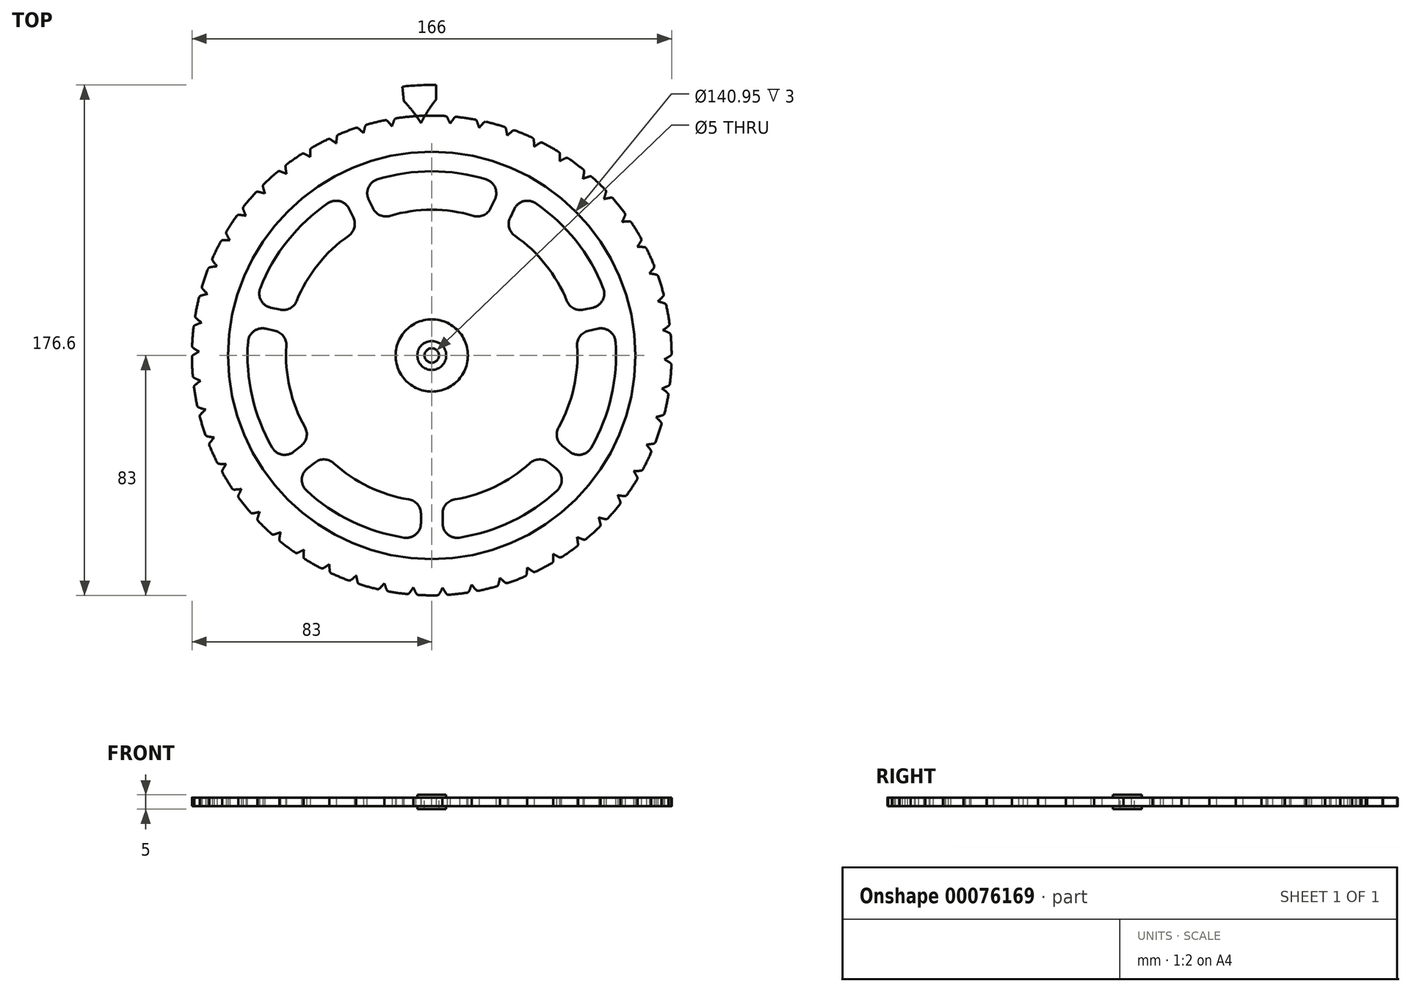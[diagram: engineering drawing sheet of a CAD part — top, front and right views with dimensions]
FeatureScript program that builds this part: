
annotation { "Feature Type Name" : "Feature", "Feature Type Description" : "" }
export const myFeature = defineFeature(function(context is Context, id is Id, definition is map)
    precondition{}
    {
        {
            assignVariable(context, id + "F0", {"name" : "Mod", "anyValue" : 3 * mm});
        }
        {
            assignVariable(context, id + "F1", {"name" : "T", "anyValue" : 50});
        }
        {
            var Q0;
            Q0=qCreatedBy(makeId("Top.planeOp"),FACE);
            var sketch = newSketch(context, id + "F2", { "sketchPlane" : qUnion([Q0])});
            skCircle(sketch, "E0", {"center": v(0, 0) * mm, "radius": 70.48 * mm, "construction": true});
            skLineSegment(sketch, "E1", {"start": v(0, 0) * mm, "end": v(0, 70.48) * mm, "construction": true});
            skLineSegment(sketch, "E2.1.0", {"start": v(0, 0) * mm, "end": v(-3.07, 70.4) * mm, "construction": true});
            skLineSegment(sketch, "E2.2.0", {"start": v(0, 0) * mm, "end": v(-6.14, 70.2) * mm, "construction": true});
            skLineSegment(sketch, "E2.3.0", {"start": v(0, 0) * mm, "end": v(-9.2, 69.87) * mm, "construction": true});
            skLineSegment(sketch, "E2.4.0", {"start": v(0, 0) * mm, "end": v(-12.24, 69.4) * mm, "construction": true});
            skLineSegment(sketch, "E2.5.0", {"start": v(0, 0) * mm, "end": v(-15.25, 68.8) * mm, "construction": true});
            skLineSegment(sketch, "E2.6.0", {"start": v(0, 0) * mm, "end": v(-18.24, 68.08) * mm, "construction": true});
            skLineSegment(sketch, "E2.7.0", {"start": v(0, 0) * mm, "end": v(-21.2, 67.22) * mm, "construction": true});
            skLineSegment(sketch, "E2.8.0", {"start": v(0, 0) * mm, "end": v(-24.1, 66.23) * mm, "construction": true});
            skLineSegment(sketch, "E2.9.0", {"start": v(0, 0) * mm, "end": v(-26.97, 65.11) * mm, "construction": true});
            skLineSegment(sketch, "E2.10.0", {"start": v(0, 0) * mm, "end": v(-29.78, 63.87) * mm, "construction": true});
            skLineSegment(sketch, "E2.11.0", {"start": v(0, 0) * mm, "end": v(-32.54, 62.51) * mm, "construction": true});
            skLineSegment(sketch, "E2.12.0", {"start": v(0, 0) * mm, "end": v(-35.24, 61.03) * mm, "construction": true});
            skLineSegment(sketch, "E2.13.0", {"start": v(0, 0) * mm, "end": v(-37.87, 59.44) * mm, "construction": true});
            skLineSegment(sketch, "E2.14.0", {"start": v(0, 0) * mm, "end": v(-40.42, 57.73) * mm, "construction": true});
            skLineSegment(sketch, "E2.15.0", {"start": v(0, 0) * mm, "end": v(-42.9, 55.91) * mm, "construction": true});
            skLineSegment(sketch, "E2.16.0", {"start": v(0, 0) * mm, "end": v(-45.3, 53.99) * mm, "construction": true});
            skLineSegment(sketch, "E2.17.0", {"start": v(0, 0) * mm, "end": v(-47.61, 51.96) * mm, "construction": true});
            skLineSegment(sketch, "E2.18.0", {"start": v(0, 0) * mm, "end": v(-49.83, 49.83) * mm, "construction": true});
            skLineSegment(sketch, "E2.19.0", {"start": v(0, 0) * mm, "end": v(-51.96, 47.61) * mm, "construction": true});
            skLineSegment(sketch, "E2.20.0", {"start": v(0, 0) * mm, "end": v(-53.99, 45.3) * mm, "construction": true});
            skLineSegment(sketch, "E2.21.0", {"start": v(0, 0) * mm, "end": v(-55.91, 42.9) * mm, "construction": true});
            skLineSegment(sketch, "E2.22.0", {"start": v(0, 0) * mm, "end": v(-57.73, 40.42) * mm, "construction": true});
            skLineSegment(sketch, "E2.23.0", {"start": v(0, 0) * mm, "end": v(-59.44, 37.87) * mm, "construction": true});
            skLineSegment(sketch, "E2.24.0", {"start": v(0, 0) * mm, "end": v(-61.03, 35.24) * mm, "construction": true});
            skLineSegment(sketch, "E2.anchor2", {"start": v(0, 0) * mm, "end": v(-67.22, 21.2) * mm, "construction": true});
            skLineSegment(sketch, "E3", {"start": v(-3.07, 70.4) * mm, "end": v(0, 70.54) * mm, "construction": true});
            skLineSegment(sketch, "E4", {"start": v(-6.14, 70.2) * mm, "end": v(-0.02, 70.74) * mm, "construction": true});
            skLineSegment(sketch, "E5", {"start": v(-9.2, 69.87) * mm, "end": v(-0.05, 71.08) * mm, "construction": true});
            skLineSegment(sketch, "E6", {"start": v(-12.24, 69.4) * mm, "end": v(-0.12, 71.54) * mm, "construction": true});
            skLineSegment(sketch, "E7", {"start": v(-15.25, 68.8) * mm, "end": v(-0.24, 72.13) * mm, "construction": true});
            skLineSegment(sketch, "E8", {"start": v(-18.24, 68.08) * mm, "end": v(-0.42, 72.85) * mm, "construction": true});
            skLineSegment(sketch, "E9", {"start": v(-21.2, 67.22) * mm, "end": v(-0.66, 73.69) * mm, "construction": true});
            skLineSegment(sketch, "E10", {"start": v(-24.1, 66.23) * mm, "end": v(-0.99, 74.64) * mm, "construction": true});
            skLineSegment(sketch, "E11", {"start": v(-26.97, 65.11) * mm, "end": v(-1.4, 75.7) * mm, "construction": true});
            skLineSegment(sketch, "E12", {"start": v(-29.78, 63.87) * mm, "end": v(-1.91, 76.87) * mm, "construction": true});
            skLineSegment(sketch, "E13", {"start": v(-32.54, 62.51) * mm, "end": v(-2.54, 78.13) * mm, "construction": true});
            skLineSegment(sketch, "E14", {"start": v(-35.24, 61.03) * mm, "end": v(-3.28, 79.49) * mm, "construction": true});
            skLineSegment(sketch, "E15", {"start": v(-37.87, 59.44) * mm, "end": v(-4.15, 80.92) * mm, "construction": true});
            skLineSegment(sketch, "E16", {"start": v(-40.42, 57.73) * mm, "end": v(-5.16, 82.42) * mm, "construction": true});
            skLineSegment(sketch, "E17", {"start": v(-42.9, 55.91) * mm, "end": v(-6.3, 84) * mm, "construction": true});
            skLineSegment(sketch, "E18", {"start": v(-45.3, 53.99) * mm, "end": v(-7.61, 85.62) * mm, "construction": true});
            skLineSegment(sketch, "E19", {"start": v(-47.61, 51.96) * mm, "end": v(-9.07, 87.28) * mm, "construction": true});
            skLineSegment(sketch, "E20", {"start": v(-49.83, 49.83) * mm, "end": v(-10.7, 88.97) * mm, "construction": true});
            skLineSegment(sketch, "E21", {"start": v(-51.96, 47.61) * mm, "end": v(-12.49, 90.7) * mm, "construction": true});
            skLineSegment(sketch, "E22", {"start": v(-53.99, 45.3) * mm, "end": v(-14.46, 92.42) * mm, "construction": true});
            skLineSegment(sketch, "E23", {"start": v(-55.91, 42.9) * mm, "end": v(-16.6, 94.14) * mm, "construction": true});
            skLineSegment(sketch, "E24", {"start": v(-57.73, 40.42) * mm, "end": v(-18.93, 95.84) * mm, "construction": true});
            skLineSegment(sketch, "E25", {"start": v(-59.44, 37.87) * mm, "end": v(-21.44, 97.52) * mm, "construction": true});
            skCircle(sketch, "E26", {"center": v(0, 0) * mm, "radius": 75 * mm});
            skCircle(sketch, "E27", {"center": v(0, 0) * mm, "radius": 78 * mm});
            skPoint(sketch, "E28", {"position": v(-1.12, 75) * mm});
            skLineSegment(sketch, "E29", {"start": v(-1.12, 75) * mm, "end": v(0, 0) * mm, "construction": true});
            skLineSegment(sketch, "E30", {"start": v(-3.61, 77.92) * mm, "end": v(0, 0) * mm, "construction": true});
            skLineSegment(sketch, "E31", {"start": v(-6.52, 70.17) * mm, "end": v(0, 0) * mm, "construction": true});
            skLineSegment(sketch, "E32.2.25.0", {"start": v(0, 0) * mm, "end": v(-62.51, 32.54) * mm, "construction": true});
            skLineSegment(sketch, "E32.2.26.0", {"start": v(0, 0) * mm, "end": v(-63.87, 29.78) * mm, "construction": true});
            skLineSegment(sketch, "E32.2.27.0", {"start": v(0, 0) * mm, "end": v(-65.11, 26.97) * mm, "construction": true});
            skLineSegment(sketch, "E32.2.28.0", {"start": v(0, 0) * mm, "end": v(-66.23, 24.1) * mm, "construction": true});
            skLineSegment(sketch, "E33", {"start": v(-61.03, 35.24) * mm, "end": v(-24.13, 99.15) * mm, "construction": true});
            skLineSegment(sketch, "E34", {"start": v(-62.51, 32.54) * mm, "end": v(-27.02, 100.73) * mm, "construction": true});
            skLineSegment(sketch, "E35", {"start": v(-63.87, 29.78) * mm, "end": v(-30.08, 102.25) * mm, "construction": true});
            skLineSegment(sketch, "E36", {"start": v(-65.11, 26.97) * mm, "end": v(-33.34, 103.68) * mm, "construction": true});
            skLineSegment(sketch, "E37", {"start": v(-66.23, 24.1) * mm, "end": v(-36.78, 105.02) * mm, "construction": true});
            skLineSegment(sketch, "E38", {"start": v(-67.22, 21.2) * mm, "end": v(-40.4, 106.24) * mm, "construction": true});
            skFitSpline(sketch, "E39", {"points": [v(0, 70.48) * mm, v(0, 70.54) * mm, v(-0.02, 70.74) * mm, v(-0.05, 71.08) * mm, v(-0.12, 71.54) * mm, v(-0.24, 72.13) * mm, v(-0.42, 72.85) * mm, v(-0.66, 73.69) * mm, v(-0.99, 74.64) * mm, v(-1.4, 75.7) * mm, v(-1.91, 76.87) * mm, v(-2.54, 78.13) * mm, v(-3.28, 79.49) * mm, v(-4.15, 80.92) * mm, v(-5.16, 82.42) * mm, v(-6.3, 84) * mm, v(-7.61, 85.62) * mm, v(-9.07, 87.28) * mm, v(-10.7, 88.97) * mm, v(-12.49, 90.7) * mm, v(-14.46, 92.42) * mm, v(-16.6, 94.14) * mm, v(-18.93, 95.84) * mm, v(-21.44, 97.52) * mm, v(-24.13, 99.15) * mm, v(-27.02, 100.73) * mm, v(-30.08, 102.25) * mm, v(-33.34, 103.68) * mm, v(-36.78, 105.02) * mm, v(-40.4, 106.24) * mm], "startDerivative": vector(-0.86, 29.64) * mm, "endDerivative": vector(-211.97, 71.92) * mm, "construction": true});
            skFitSpline(sketch, "E40.MirrorCS", {"points": [v(-6.52, 70.17) * mm, v(-6.52, 70.24) * mm, v(-6.53, 70.44) * mm, v(-6.52, 70.78) * mm, v(-6.5, 71.25) * mm, v(-6.43, 71.85) * mm, v(-6.32, 72.58) * mm, v(-6.16, 73.43) * mm, v(-5.92, 74.41) * mm, v(-5.6, 75.5) * mm, v(-5.2, 76.72) * mm, v(-4.7, 78.03) * mm, v(-4.09, 79.45) * mm, v(-3.35, 80.96) * mm, v(-2.49, 82.55) * mm, v(-1.49, 84.22) * mm, v(-0.34, 85.95) * mm, v(0.96, 87.74) * mm, v(2.42, 89.58) * mm, v(4.04, 91.46) * mm, v(5.84, 93.36) * mm, v(7.82, 95.27) * mm, v(9.98, 97.18) * mm, v(12.32, 99.08) * mm, v(14.86, 100.96) * mm, v(17.58, 102.8) * mm, v(20.5, 104.6) * mm, v(23.6, 106.32) * mm, v(26.9, 107.97) * mm, v(30.4, 109.53) * mm], "startDerivative": vector(-1.88, 29.59) * mm, "endDerivative": vector(204.4, 91.22) * mm, "construction": true});
            skFitSpline(sketch, "E41.0", {"points": [v(-6.9, 84.29) * mm, v(-6.9, 84.34) * mm, v(-6.9, 84.36) * mm, v(-6.9, 84.36) * mm, v(-6.9, 84.38) * mm, v(-6.9, 84.43) * mm, v(-6.9, 84.53) * mm, v(-6.9, 84.64) * mm, v(-6.9, 84.77) * mm, v(-6.9, 84.94) * mm, v(-6.88, 85.16) * mm, v(-6.86, 85.4) * mm, v(-6.84, 85.67) * mm, v(-6.8, 86.03) * mm, v(-6.74, 86.5) * mm, v(-6.64, 87.12) * mm, v(-6.5, 87.76) * mm, v(-6.3, 88.66) * mm, v(-6, 89.84) * mm, v(-5.52, 91.34) * mm, v(-4.95, 92.89) * mm, v(-4.27, 94.5) * mm, v(-3.5, 96.13) * mm, v(-2.34, 98.36) * mm, v(-0.65, 101.19) * mm, v(1.75, 104.61) * mm, v(4.5, 108.02) * mm, v(7.1, 110.82) * mm, v(9.33, 113) * mm, v(11.1, 114.63) * mm, v(12.93, 116.22) * mm, v(14.85, 117.78) * mm, v(16.84, 119.3) * mm, v(18.91, 120.79) * mm, v(20.68, 121.99) * mm, v(22.15, 122.93) * mm, v(23.28, 123.63) * mm, v(24.42, 124.32) * mm, v(25.37, 124.88) * mm, v(26.12, 125.3) * mm, v(26.85, 125.73) * mm, v(27.6, 126.14) * mm, v(28.38, 126.56) * mm, v(29, 126.9) * mm, v(29.68, 127.23) * mm, v(30.4, 127.6) * mm, v(31.14, 127.96) * mm, v(31.86, 128.3) * mm, v(32.52, 128.63) * mm, v(33.1, 128.9) * mm, v(33.47, 129.08) * mm, v(33.69, 129.18) * mm, v(33.85, 129.26) * mm, v(33.98, 129.32) * mm, v(34.16, 129.4) * mm, v(34.5, 129.54) * mm, v(35.34, 129.9) * mm, v(36.59, 130.44) * mm, v(37.87, 131) * mm]});
            skFitSpline(sketch, "E42.0", {"points": [v(-0.05, 84.57) * mm, v(-0.05, 84.62) * mm, v(-0.05, 84.64) * mm, v(-0.05, 84.64) * mm, v(-0.05, 84.66) * mm, v(-0.06, 84.71) * mm, v(-0.06, 84.81) * mm, v(-0.07, 84.92) * mm, v(-0.08, 85.05) * mm, v(-0.1, 85.22) * mm, v(-0.13, 85.44) * mm, v(-0.17, 85.68) * mm, v(-0.22, 85.94) * mm, v(-0.28, 86.3) * mm, v(-0.39, 86.77) * mm, v(-0.54, 87.37) * mm, v(-0.72, 88) * mm, v(-0.99, 88.88) * mm, v(-1.4, 90.03) * mm, v(-2, 91.48) * mm, v(-2.7, 92.98) * mm, v(-3.5, 94.52) * mm, v(-4.4, 96.1) * mm, v(-5.74, 98.22) * mm, v(-7.65, 100.9) * mm, v(-10.33, 104.12) * mm, v(-13.36, 107.29) * mm, v(-16.17, 109.86) * mm, v(-18.58, 111.86) * mm, v(-20.46, 113.33) * mm, v(-22.43, 114.76) * mm, v(-24.47, 116.16) * mm, v(-26.58, 117.52) * mm, v(-28.76, 118.83) * mm, v(-30.63, 119.88) * mm, v(-32.16, 120.7) * mm, v(-33.35, 121.3) * mm, v(-34.55, 121.9) * mm, v(-35.54, 122.38) * mm, v(-36.31, 122.74) * mm, v(-37.08, 123.1) * mm, v(-37.85, 123.45) * mm, v(-38.67, 123.8) * mm, v(-39.32, 124.08) * mm, v(-40.02, 124.37) * mm, v(-40.77, 124.67) * mm, v(-41.53, 124.97) * mm, v(-42.28, 125.26) * mm, v(-42.97, 125.52) * mm, v(-43.56, 125.75) * mm, v(-43.95, 125.9) * mm, v(-44.18, 125.98) * mm, v(-44.34, 126.04) * mm, v(-44.48, 126.1) * mm, v(-44.67, 126.16) * mm, v(-45.02, 126.28) * mm, v(-45.88, 126.56) * mm, v(-47.17, 127) * mm, v(-48.5, 127.45) * mm]});
            skArc(sketch, "E43", {"start": v(-0.13, 71.25) * mm, "mid": v(-3.3, 71.17) * mm, "end": v(-6.46, 70.96) * mm});
            skArc(sketch, "E44", {"start": v(-6.72, 70.93) * mm, "mid": v(3.3, -71.17) * mm, "end": v(0.13, 71.25) * mm});
            skPoint(sketch, "E45.visualSharp", {"position": v(-6.46, 70.96) * mm});
            skArc(sketch, "E45.filletArc", {"start": v(-6.72, 70.93) * mm, "mid": v(-6.53, 71.02) * mm, "end": v(-6.45, 71.2) * mm});
            skPoint(sketch, "E46.visualSharp", {"position": v(-0.13, 71.25) * mm});
            skArc(sketch, "E46.filletArc", {"start": v(-0.17, 71.5) * mm, "mid": v(-0.07, 71.32) * mm, "end": v(0.13, 71.25) * mm});
            skArc(sketch, "E47", {"start": v(-6.72, 70.93) * mm, "mid": v(-3.3, 71.17) * mm, "end": v(0.13, 71.25) * mm});
            skSolve(sketch);
        }
        {
            assignVariable(context, id + "F3", {"name" : "Thickness", "anyValue" : 3 * mm});
        }
        {
            var Q0;
            {var subQ0=sQuery(id+"F2.wireOp",EDGE,"E44");Q0=makeQuery(id+"F2.imprint","IMPRINT",FACE,{"disambiguationData":[TD([[makeQuery(id+"F2.imprint","IMPRINT",EDGE,{"derivedFrom":subQ0}),1.0]])]});}
            extrude(context, id + "F4", {"entities" : qUnion([Q0]), "endBound" : BoundingType.SYMMETRIC, "depth" : getVariable(context, 'Thickness')});
        }
        {
            var Q0;
            {var subQ0=sQuery(id+"F2.wireOp",EDGE,"E41.0");var subQ1=sQuery(id+"F2.wireOp",EDGE,"E26");var subQ2=makeQuery(id+"F2.imprint","INTERSECT",VERTEX,{"derivedFrom":[subQ1,subQ0]});Q0=makeQuery(id+"F2.imprint","IMPRINT",FACE,{"disambiguationData":[TD([[makeQuery(id+"F2.imprint","IMPRINT",EDGE,{"disambiguationData":[TD([[subQ2,1.0]])],"derivedFrom":subQ1}),-1.0]])]});}
            var Q1;
            {var subQ0=sQuery(id+"F2.wireOp",EDGE,"E45.filletArc");Q1=makeQuery(id+"F2.imprint","IMPRINT",FACE,{"disambiguationData":[TD([[makeQuery(id+"F2.imprint","IMPRINT",EDGE,{"derivedFrom":subQ0}),-1.0]])]});}
            extrude(context, id + "F5", {"entities" : qUnion([Q0, Q1]), "endBound" : BoundingType.SYMMETRIC, "oppositeDirection" : true, "depth" : getVariable(context, 'Thickness')});
        }
        {
            var Q0;
            Q0=qCreatedBy(makeId("Front.planeOp"),FACE);
            var sketch = newSketch(context, id + "F6", { "sketchPlane" : qUnion([Q0])});
            skLineSegment(sketch, "E48", {"start": v(0, 0) * mm, "end": v(0, 11.67) * mm});
            skSolve(sketch);
        }
        {
            var Q0;
            Q0=makeQuery(id+"F5.opExtrude","SWEPT_BODY",BODY,{"disambiguationData":[OSD([sQuery(id+"F2.wireOp",EDGE,"4a69cfca-a3bc-48ab-be35-960da39a462e"),sQuery(id+"F2.wireOp",EDGE,"Aigjkfxe-bQmJ-sPwt-LIfV-hiAVdCM8k71b"),sQuery(id+"F2.wireOp",EDGE,"E27"),sQuery(id+"F2.wireOp",EDGE,"abf2ab3a-d2cd-41dc-bda2-9d514d4bd3180.MirrorCS"),sQuery(id+"F2.wireOp",EDGE,"dKfRnCup-fbZC-EHfO-hmoI-6kX9ckiFD719"),sQuery(id+"F2.wireOp",EDGE,"V1zgMlGZ-DbEQ-ZBOL-SlYs-zCFJA2V7msXA")])]});
            var Q1;
            Q1=sQuery(id+"F6.wireOp",EDGE,"E48");
            circularPattern(context, id + "F7", {"operationType" : NewBodyOperationType.ADD, "entities" : qUnion([Q0]), "axis" : qUnion([Q1]), "angle" : 360 * degree, "instanceCount" : getVariable(context, 'T'), "equalSpace" : true});
        }
        {
            var Q0;
            Q0=qCreatedBy(makeId("Top.planeOp"),FACE);
            var sketch = newSketch(context, id + "F8", { "sketchPlane" : qUnion([Q0])});
            skCircle(sketch, "E49", {"center": v(0, 0) * mm, "radius": 71.25 * mm});
            skCircle(sketch, "E50", {"center": v(0, 0) * mm, "radius": 2.5 * mm});
            skCircle(sketch, "E51", {"center": v(0, 0) * mm, "radius": 5 * mm});
            skCircle(sketch, "E52.0", {"center": v(0, 0) * mm, "radius": 63.75 * mm, "construction": true});
            skCircle(sketch, "E53.0", {"center": v(0, 0) * mm, "radius": 12.5 * mm, "construction": true});
            skLineSegment(sketch, "E54", {"start": v(0, 0) * mm, "end": v(30.91, 64.2) * mm, "construction": true});
            skLineSegment(sketch, "E55", {"start": v(2.68, 14.2) * mm, "end": v(6.09, 21.28) * mm});
            skArc(sketch, "E56", {"start": v(0, 12.5) * mm, "mid": v(0.01, -12.5) * mm, "end": v(-0.02, 12.5) * mm});
            skArc(sketch, "E57", {"start": v(0, 63.75) * mm, "mid": v(9.5, 63.04) * mm, "end": v(18.8, 60.92) * mm});
            skPoint(sketch, "E58.visualSharp", {"position": v(24.23, 58.96) * mm});
            skPoint(sketch, "E59.visualSharp", {"position": v(1.8, 12.37) * mm});
            skArc(sketch, "E59.filletArc", {"start": v(-0.02, 12.5) * mm, "mid": v(1.57, 12.96) * mm, "end": v(2.68, 14.2) * mm});
            skCircle(sketch, "E60", {"center": v(0, 0) * mm, "radius": 46.67 * mm, "construction": true});
            skPoint(sketch, "E61", {"position": v(0, 46.67) * mm});
            skArc(sketch, "E62", {"start": v(0, 50.42) * mm, "mid": v(7.3, 49.89) * mm, "end": v(14.43, 48.3) * mm});
            skLineSegment(sketch, "E63", {"start": v(18.44, 46.93) * mm, "end": v(18.44, 46.93) * mm});
            skLineSegment(sketch, "E64", {"start": v(20.36, 50.93) * mm, "end": v(21.83, 53.97) * mm});
            skPoint(sketch, "E65.visualSharp", {"position": v(18.44, 46.93) * mm});
            skArc(sketch, "E65.filletArc", {"start": v(14.43, 48.3) * mm, "mid": v(17.88, 48.53) * mm, "end": v(20.36, 50.93) * mm});
            skLineSegment(sketch, "E66", {"start": v(0, 12.5) * mm, "end": v(0, 29.58) * mm, "construction": true});
            skLineSegment(sketch, "E67", {"start": v(0, 29.58) * mm, "end": v(0, 46.67) * mm, "construction": true});
            skLineSegment(sketch, "E68", {"start": v(0, 46.67) * mm, "end": v(0, 63.75) * mm, "construction": true});
            skCircle(sketch, "E69", {"center": v(0, 0) * mm, "radius": 29.58 * mm, "construction": true});
            skArc(sketch, "E70", {"start": v(0, 25.83) * mm, "mid": v(1.92, 25.76) * mm, "end": v(3.83, 25.55) * mm});
            skPoint(sketch, "E71.visualSharp", {"position": v(7.71, 24.66) * mm});
            skArc(sketch, "E71.filletArc", {"start": v(6.09, 21.28) * mm, "mid": v(6.03, 23.98) * mm, "end": v(3.83, 25.55) * mm});
            skLineSegment(sketch, "E72", {"start": v(3.75, 38.14) * mm, "end": v(3.75, 36.52) * mm});
            skArc(sketch, "E73", {"start": v(6.92, 32.6) * mm, "mid": v(10.77, 31.55) * mm, "end": v(14.46, 30.03) * mm});
            skArc(sketch, "E74", {"start": v(8.55, 42.06) * mm, "mid": v(13.69, 40.67) * mm, "end": v(18.62, 38.67) * mm});
            skPoint(sketch, "E75.visualSharp", {"position": v(3.75, 33.12) * mm});
            skArc(sketch, "E75.filletArc", {"start": v(3.75, 36.52) * mm, "mid": v(4.64, 34) * mm, "end": v(6.92, 32.6) * mm});
            skPoint(sketch, "E76.visualSharp", {"position": v(3.75, 42.75) * mm});
            skArc(sketch, "E76.filletArc", {"start": v(8.55, 42.06) * mm, "mid": v(5.22, 41.23) * mm, "end": v(3.75, 38.14) * mm});
            skArc(sketch, "E77.MirrorCS", {"start": v(-14.43, 48.3) * mm, "mid": v(-17.88, 48.53) * mm, "end": v(-20.36, 50.93) * mm});
            skArc(sketch, "E78.MirrorCS", {"start": v(0, 50.42) * mm, "mid": v(-7.3, 49.89) * mm, "end": v(-14.43, 48.3) * mm});
            skArc(sketch, "E79.MirrorCS", {"start": v(-8.55, 42.06) * mm, "mid": v(-13.69, 40.67) * mm, "end": v(-18.62, 38.67) * mm});
            skArc(sketch, "E80.MirrorCS", {"start": v(-8.55, 42.06) * mm, "mid": v(-5.22, 41.23) * mm, "end": v(-3.75, 38.14) * mm});
            skLineSegment(sketch, "E81.MirrorCS", {"start": v(-3.75, 38.14) * mm, "end": v(-3.75, 36.52) * mm});
            skArc(sketch, "E82.MirrorCS", {"start": v(-3.75, 36.52) * mm, "mid": v(-4.64, 34) * mm, "end": v(-6.92, 32.6) * mm});
            skArc(sketch, "E83.MirrorCS", {"start": v(-6.92, 32.6) * mm, "mid": v(-10.77, 31.55) * mm, "end": v(-14.46, 30.03) * mm});
            skArc(sketch, "E84.MirrorCS", {"start": v(-6.09, 21.28) * mm, "mid": v(-6.03, 23.98) * mm, "end": v(-3.83, 25.55) * mm});
            skArc(sketch, "E85.MirrorCS", {"start": v(0, 25.83) * mm, "mid": v(-1.92, 25.76) * mm, "end": v(-3.83, 25.55) * mm});
            skLineSegment(sketch, "E86.MirrorCS", {"start": v(-2.68, 14.2) * mm, "end": v(-6.09, 21.28) * mm});
            skArc(sketch, "E87.MirrorCS", {"start": v(0.02, 12.5) * mm, "mid": v(-1.57, 12.96) * mm, "end": v(-2.68, 14.2) * mm});
            skArc(sketch, "E88.MirrorCS", {"start": v(0, 12.5) * mm, "mid": v(-0.01, -12.5) * mm, "end": v(0.02, 12.5) * mm});
            skArc(sketch, "E89.filletArc", {"start": v(21.83, 53.97) * mm, "mid": v(21.9, 58.14) * mm, "end": v(18.8, 60.92) * mm});
            skArc(sketch, "E90.MirrorCS", {"start": v(-21.83, 53.97) * mm, "mid": v(-21.9, 58.14) * mm, "end": v(-18.8, 60.92) * mm});
            skArc(sketch, "E91.MirrorCS", {"start": v(0, 63.75) * mm, "mid": v(-9.5, 63.04) * mm, "end": v(-18.8, 60.92) * mm});
            skLineSegment(sketch, "E92.MirrorCS", {"start": v(-20.36, 50.93) * mm, "end": v(-21.83, 53.97) * mm});
            skPoint(sketch, "E93.1.0", {"position": v(-31, 55.71) * mm});
            skArc(sketch, "E93.1.1", {"start": v(-38.21, 19.54) * mm, "mid": v(-40.34, 14.66) * mm, "end": v(-41.84, 9.55) * mm});
            skLineSegment(sketch, "E93.1.2", {"start": v(-23.13, 18.44) * mm, "end": v(-36.49, 29.1) * mm, "construction": true});
            skLineSegment(sketch, "E93.1.3", {"start": v(-36.49, 29.1) * mm, "end": v(-49.84, 39.75) * mm, "construction": true});
            skArc(sketch, "E93.1.4", {"start": v(-39.42, 31.43) * mm, "mid": v(-34.46, 36.8) * mm, "end": v(-28.77, 41.4) * mm});
            skArc(sketch, "E93.1.5", {"start": v(-29.8, 14.92) * mm, "mid": v(-31.38, 11.25) * mm, "end": v(-32.5, 7.42) * mm});
            skArc(sketch, "E93.1.6", {"start": v(-20.2, 16.1) * mm, "mid": v(-21.34, 14.56) * mm, "end": v(-22.36, 12.94) * mm});
            skLineSegment(sketch, "E93.1.7", {"start": v(-12.77, 6.76) * mm, "end": v(-20.43, 8.5) * mm});
            skLineSegment(sketch, "E93.1.8", {"start": v(-32.15, 20.85) * mm, "end": v(-30.9, 19.84) * mm});
            skArc(sketch, "E93.1.9", {"start": v(-55.8, 16.58) * mm, "mid": v(-59.11, 19.12) * mm, "end": v(-59.35, 23.28) * mm});
            skPoint(sketch, "E93.1.10", {"position": v(-25.2, 43.67) * mm});
            skArc(sketch, "E93.1.11", {"start": v(-49.84, 39.75) * mm, "mid": v(-55.21, 31.87) * mm, "end": v(-59.35, 23.28) * mm});
            skArc(sketch, "E93.1.12", {"start": v(-39.42, 31.43) * mm, "mid": v(-43.55, 25.4) * mm, "end": v(-46.76, 18.84) * mm});
            skPoint(sketch, "E93.1.13", {"position": v(-31.09, 29.59) * mm});
            skLineSegment(sketch, "E93.1.14", {"start": v(-9.77, 7.8) * mm, "end": v(-23.13, 18.44) * mm, "construction": true});
            skArc(sketch, "E93.1.15", {"start": v(-27.55, 32.9) * mm, "mid": v(-23.27, 36.06) * mm, "end": v(-18.62, 38.67) * mm});
            skPoint(sketch, "E93.1.16", {"position": v(-36.49, 29.1) * mm});
            skLineSegment(sketch, "E93.1.17", {"start": v(-9.43, 10.94) * mm, "end": v(-12.84, 18.03) * mm});
            skArc(sketch, "E93.1.18", {"start": v(-49.84, 39.75) * mm, "mid": v(-43.36, 46.73) * mm, "end": v(-35.9, 52.68) * mm});
            skLineSegment(sketch, "E93.1.19", {"start": v(-52.52, 15.83) * mm, "end": v(-55.8, 16.58) * mm});
            skPoint(sketch, "E93.1.20", {"position": v(-14.47, 21.4) * mm});
            skArc(sketch, "E93.1.21", {"start": v(-21.18, 25.74) * mm, "mid": v(-17.95, 28.09) * mm, "end": v(-14.46, 30.03) * mm});
            skPoint(sketch, "E93.1.22", {"position": v(-8.55, 9.12) * mm});
            skPoint(sketch, "E93.1.23", {"position": v(-23.56, 23.58) * mm});
            skArc(sketch, "E93.1.24", {"start": v(-28.77, 41.4) * mm, "mid": v(-26.8, 44.23) * mm, "end": v(-27.12, 47.68) * mm});
            skLineSegment(sketch, "E93.1.25", {"start": v(-27.48, 26.71) * mm, "end": v(-26.21, 25.7) * mm});
            skArc(sketch, "E93.1.26", {"start": v(-20.2, 16.1) * mm, "mid": v(-18.95, 17.56) * mm, "end": v(-17.59, 18.92) * mm});
            skPoint(sketch, "E93.1.27", {"position": v(-31, 55.71) * mm});
            skArc(sketch, "E93.1.28", {"start": v(-27.55, 32.9) * mm, "mid": v(-28.98, 29.79) * mm, "end": v(-27.48, 26.71) * mm});
            skArc(sketch, "E93.1.29", {"start": v(-26.21, 25.7) * mm, "mid": v(-23.69, 24.83) * mm, "end": v(-21.18, 25.74) * mm});
            skLineSegment(sketch, "E93.1.30", {"start": v(-27.12, 47.68) * mm, "end": v(-28.59, 50.71) * mm});
            skArc(sketch, "E93.1.31", {"start": v(-28.59, 50.71) * mm, "mid": v(-31.8, 53.37) * mm, "end": v(-35.9, 52.68) * mm});
            skArc(sketch, "E93.1.32", {"start": v(-9.76, 7.81) * mm, "mid": v(-11.11, 6.85) * mm, "end": v(-12.77, 6.76) * mm});
            skArc(sketch, "E93.1.33", {"start": v(-20.43, 8.5) * mm, "mid": v(-22.51, 10.24) * mm, "end": v(-22.36, 12.94) * mm});
            skArc(sketch, "E93.1.34", {"start": v(-38.21, 19.54) * mm, "mid": v(-35.5, 21.63) * mm, "end": v(-32.15, 20.85) * mm});
            skArc(sketch, "E93.1.35", {"start": v(-30.9, 19.84) * mm, "mid": v(-29.48, 17.57) * mm, "end": v(-29.8, 14.92) * mm});
            skArc(sketch, "E93.1.36", {"start": v(-12.84, 18.03) * mm, "mid": v(-14.99, 19.67) * mm, "end": v(-17.59, 18.92) * mm});
            skArc(sketch, "E93.1.37", {"start": v(-46.76, 18.84) * mm, "mid": v(-49.09, 16.28) * mm, "end": v(-52.52, 15.83) * mm});
            skArc(sketch, "E93.1.38", {"start": v(-9.79, 7.78) * mm, "mid": v(-9.15, 9.3) * mm, "end": v(-9.43, 10.94) * mm});
            skArc(sketch, "E93.1.39", {"start": v(-9.77, 7.8) * mm, "mid": v(9.77, -7.8) * mm, "end": v(-9.76, 7.81) * mm});
            skArc(sketch, "E93.1.40", {"start": v(-9.77, 7.8) * mm, "mid": v(9.78, -7.78) * mm, "end": v(-9.79, 7.78) * mm});
            skPoint(sketch, "E93.2.0", {"position": v(-62.88, 10.5) * mm});
            skArc(sketch, "E93.2.1", {"start": v(-39.1, -17.7) * mm, "mid": v(-36.6, -22.4) * mm, "end": v(-33.55, -26.76) * mm});
            skLineSegment(sketch, "E93.2.2", {"start": v(-28.84, -6.58) * mm, "end": v(-45.5, -10.38) * mm, "construction": true});
            skLineSegment(sketch, "E93.2.3", {"start": v(-45.5, -10.38) * mm, "end": v(-62.15, -14.19) * mm, "construction": true});
            skArc(sketch, "E93.2.4", {"start": v(-49.15, -11.22) * mm, "mid": v(-50.26, -4) * mm, "end": v(-50.3, 3.32) * mm});
            skArc(sketch, "E93.2.5", {"start": v(-30.25, -14) * mm, "mid": v(-28.36, -17.52) * mm, "end": v(-26.06, -20.78) * mm});
            skArc(sketch, "E93.2.6", {"start": v(-25.19, -5.75) * mm, "mid": v(-24.69, -7.6) * mm, "end": v(-24.06, -9.42) * mm});
            skLineSegment(sketch, "E93.2.7", {"start": v(-13.25, -5.77) * mm, "end": v(-19.4, -10.67) * mm});
            skLineSegment(sketch, "E93.2.8", {"start": v(-36.35, -12.14) * mm, "end": v(-34.77, -11.78) * mm});
            skArc(sketch, "E93.2.9", {"start": v(-47.76, -33.29) * mm, "mid": v(-51.8, -34.3) * mm, "end": v(-55.2, -31.88) * mm});
            skPoint(sketch, "E93.2.10", {"position": v(-49.85, 7.53) * mm});
            skArc(sketch, "E93.2.11", {"start": v(-62.15, -14.19) * mm, "mid": v(-59.34, -23.3) * mm, "end": v(-55.2, -31.88) * mm});
            skArc(sketch, "E93.2.12", {"start": v(-49.15, -11.22) * mm, "mid": v(-47.01, -18.2) * mm, "end": v(-43.89, -24.82) * mm});
            skPoint(sketch, "E93.2.13", {"position": v(-42.52, -5.86) * mm});
            skLineSegment(sketch, "E93.2.14", {"start": v(-12.19, -2.78) * mm, "end": v(-28.84, -6.58) * mm, "construction": true});
            skArc(sketch, "E93.2.15", {"start": v(-42.9, -1.03) * mm, "mid": v(-42.7, 4.3) * mm, "end": v(-41.84, 9.55) * mm});
            skPoint(sketch, "E93.2.16", {"position": v(-45.5, -10.38) * mm});
            skLineSegment(sketch, "E93.2.17", {"start": v(-14.44, -0.55) * mm, "end": v(-22.1, 1.2) * mm});
            skArc(sketch, "E93.2.18", {"start": v(-62.15, -14.19) * mm, "mid": v(-63.57, -4.76) * mm, "end": v(-63.57, 4.77) * mm});
            skLineSegment(sketch, "E93.2.19", {"start": v(-45.12, -31.19) * mm, "end": v(-47.76, -33.29) * mm});
            skPoint(sketch, "E93.2.20", {"position": v(-25.75, 2.03) * mm});
            skArc(sketch, "E93.2.21", {"start": v(-33.33, -0.5) * mm, "mid": v(-33.15, 3.48) * mm, "end": v(-32.5, 7.42) * mm});
            skPoint(sketch, "E93.2.22", {"position": v(-12.46, -1) * mm});
            skPoint(sketch, "E93.2.23", {"position": v(-33.13, -3.71) * mm});
            skArc(sketch, "E93.2.24", {"start": v(-50.3, 3.32) * mm, "mid": v(-51.29, 6.63) * mm, "end": v(-54.18, 8.52) * mm});
            skLineSegment(sketch, "E93.2.25", {"start": v(-38.02, -4.83) * mm, "end": v(-36.44, -4.47) * mm});
            skArc(sketch, "E93.2.26", {"start": v(-25.19, -5.75) * mm, "mid": v(-25.54, -3.86) * mm, "end": v(-25.76, -1.95) * mm});
            skPoint(sketch, "E93.2.27", {"position": v(-62.88, 10.5) * mm});
            skArc(sketch, "E93.2.28", {"start": v(-42.9, -1.03) * mm, "mid": v(-41.36, -4.09) * mm, "end": v(-38.02, -4.83) * mm});
            skArc(sketch, "E93.2.29", {"start": v(-36.44, -4.47) * mm, "mid": v(-34.18, -3.04) * mm, "end": v(-33.33, -0.5) * mm});
            skLineSegment(sketch, "E93.2.30", {"start": v(-54.18, 8.52) * mm, "end": v(-57.47, 9.27) * mm});
            skArc(sketch, "E93.2.31", {"start": v(-57.47, 9.27) * mm, "mid": v(-61.55, 8.42) * mm, "end": v(-63.57, 4.77) * mm});
            skArc(sketch, "E93.2.32", {"start": v(-12.2, -2.76) * mm, "mid": v(-12.29, -4.42) * mm, "end": v(-13.25, -5.77) * mm});
            skArc(sketch, "E93.2.33", {"start": v(-19.4, -10.67) * mm, "mid": v(-22.04, -11.22) * mm, "end": v(-24.06, -9.42) * mm});
            skArc(sketch, "E93.2.34", {"start": v(-39.1, -17.7) * mm, "mid": v(-39.04, -14.26) * mm, "end": v(-36.35, -12.14) * mm});
            skArc(sketch, "E93.2.35", {"start": v(-34.77, -11.78) * mm, "mid": v(-32.12, -12.1) * mm, "end": v(-30.25, -14) * mm});
            skArc(sketch, "E93.2.36", {"start": v(-22.1, 1.2) * mm, "mid": v(-24.73, 0.55) * mm, "end": v(-25.76, -1.95) * mm});
            skArc(sketch, "E93.2.37", {"start": v(-43.89, -24.82) * mm, "mid": v(-43.33, -28.23) * mm, "end": v(-45.12, -31.19) * mm});
            skArc(sketch, "E93.2.38", {"start": v(-12.18, -2.8) * mm, "mid": v(-12.99, -1.35) * mm, "end": v(-14.44, -0.55) * mm});
            skArc(sketch, "E93.2.39", {"start": v(-12.19, -2.78) * mm, "mid": v(12.19, 2.77) * mm, "end": v(-12.2, -2.76) * mm});
            skArc(sketch, "E93.2.40", {"start": v(-12.19, -2.78) * mm, "mid": v(12.18, 2.8) * mm, "end": v(-12.18, -2.8) * mm});
            skPoint(sketch, "E93.3.0", {"position": v(-47.42, -42.61) * mm});
            skArc(sketch, "E93.3.1", {"start": v(-10.55, -41.6) * mm, "mid": v(-5.31, -42.59) * mm, "end": v(0, -42.92) * mm});
            skLineSegment(sketch, "E93.3.2", {"start": v(-12.84, -26.65) * mm, "end": v(-20.25, -42.05) * mm, "construction": true});
            skLineSegment(sketch, "E93.3.3", {"start": v(-20.25, -42.05) * mm, "end": v(-27.66, -57.44) * mm, "construction": true});
            skArc(sketch, "E93.3.4", {"start": v(-21.87, -45.42) * mm, "mid": v(-28.21, -41.78) * mm, "end": v(-33.96, -37.26) * mm});
            skArc(sketch, "E93.3.5", {"start": v(-7.91, -32.38) * mm, "mid": v(-3.99, -33.1) * mm, "end": v(0, -33.33) * mm});
            skArc(sketch, "E93.3.6", {"start": v(-11.2, -23.28) * mm, "mid": v(-9.45, -24.04) * mm, "end": v(-7.64, -24.68) * mm});
            skLineSegment(sketch, "E93.3.7", {"start": v(-3.75, -13.95) * mm, "end": v(-3.75, -21.81) * mm});
            skLineSegment(sketch, "E93.3.8", {"start": v(-13.17, -35.99) * mm, "end": v(-12.47, -34.53) * mm});
            skArc(sketch, "E93.3.9", {"start": v(-3.75, -58.1) * mm, "mid": v(-5.49, -61.88) * mm, "end": v(-9.5, -63.04) * mm});
            skPoint(sketch, "E93.3.10", {"position": v(-36.97, -34.28) * mm});
            skArc(sketch, "E93.3.11", {"start": v(-27.66, -57.44) * mm, "mid": v(-18.79, -60.92) * mm, "end": v(-9.5, -63.04) * mm});
            skArc(sketch, "E93.3.12", {"start": v(-21.87, -45.42) * mm, "mid": v(-15.08, -48.1) * mm, "end": v(-7.96, -49.78) * mm});
            skPoint(sketch, "E93.3.13", {"position": v(-21.93, -36.9) * mm});
            skLineSegment(sketch, "E93.3.14", {"start": v(-5.42, -11.26) * mm, "end": v(-12.84, -26.65) * mm, "construction": true});
            skArc(sketch, "E93.3.15", {"start": v(-25.95, -34.18) * mm, "mid": v(-29.98, -30.7) * mm, "end": v(-33.55, -26.76) * mm});
            skPoint(sketch, "E93.3.16", {"position": v(-20.25, -42.05) * mm});
            skLineSegment(sketch, "E93.3.17", {"start": v(-8.57, -11.63) * mm, "end": v(-14.72, -16.53) * mm});
            skArc(sketch, "E93.3.18", {"start": v(-27.66, -57.44) * mm, "mid": v(-35.91, -52.67) * mm, "end": v(-43.37, -46.73) * mm});
            skLineSegment(sketch, "E93.3.19", {"start": v(-3.75, -54.72) * mm, "end": v(-3.75, -58.1) * mm});
            skPoint(sketch, "E93.3.20", {"position": v(-17.65, -18.87) * mm});
            skArc(sketch, "E93.3.21", {"start": v(-20.38, -26.38) * mm, "mid": v(-23.39, -23.75) * mm, "end": v(-26.06, -20.78) * mm});
            skPoint(sketch, "E93.3.22", {"position": v(-6.98, -10.37) * mm});
            skPoint(sketch, "E93.3.23", {"position": v(-17.75, -28.21) * mm});
            skArc(sketch, "E93.3.24", {"start": v(-33.96, -37.26) * mm, "mid": v(-37.16, -35.96) * mm, "end": v(-40.44, -37.05) * mm});
            skLineSegment(sketch, "E93.3.25", {"start": v(-19.93, -32.73) * mm, "end": v(-19.22, -31.28) * mm});
            skArc(sketch, "E93.3.26", {"start": v(-11.2, -23.28) * mm, "mid": v(-12.9, -22.38) * mm, "end": v(-14.53, -21.36) * mm});
            skPoint(sketch, "E93.3.27", {"position": v(-47.42, -42.61) * mm});
            skArc(sketch, "E93.3.28", {"start": v(-25.95, -34.18) * mm, "mid": v(-22.6, -34.89) * mm, "end": v(-19.93, -32.73) * mm});
            skArc(sketch, "E93.3.29", {"start": v(-19.22, -31.28) * mm, "mid": v(-18.94, -28.62) * mm, "end": v(-20.38, -26.38) * mm});
            skLineSegment(sketch, "E93.3.30", {"start": v(-40.44, -37.05) * mm, "end": v(-43.08, -39.15) * mm});
            skArc(sketch, "E93.3.31", {"start": v(-43.08, -39.15) * mm, "mid": v(-44.96, -42.88) * mm, "end": v(-43.37, -46.73) * mm});
            skArc(sketch, "E93.3.32", {"start": v(-5.44, -11.25) * mm, "mid": v(-4.2, -12.36) * mm, "end": v(-3.75, -13.95) * mm});
            skArc(sketch, "E93.3.33", {"start": v(-3.75, -21.81) * mm, "mid": v(-4.97, -24.23) * mm, "end": v(-7.64, -24.68) * mm});
            skArc(sketch, "E93.3.34", {"start": v(-10.55, -41.6) * mm, "mid": v(-13.19, -39.42) * mm, "end": v(-13.17, -35.99) * mm});
            skArc(sketch, "E93.3.35", {"start": v(-12.47, -34.53) * mm, "mid": v(-10.57, -32.65) * mm, "end": v(-7.91, -32.38) * mm});
            skArc(sketch, "E93.3.36", {"start": v(-14.72, -16.53) * mm, "mid": v(-15.84, -19) * mm, "end": v(-14.53, -21.36) * mm});
            skArc(sketch, "E93.3.37", {"start": v(-7.96, -49.78) * mm, "mid": v(-4.95, -51.48) * mm, "end": v(-3.75, -54.72) * mm});
            skArc(sketch, "E93.3.38", {"start": v(-5.4, -11.27) * mm, "mid": v(-7.04, -11) * mm, "end": v(-8.57, -11.63) * mm});
            skArc(sketch, "E93.3.39", {"start": v(-5.42, -11.26) * mm, "mid": v(5.43, 11.26) * mm, "end": v(-5.44, -11.25) * mm});
            skArc(sketch, "E93.3.40", {"start": v(-5.42, -11.26) * mm, "mid": v(5.41, 11.27) * mm, "end": v(-5.4, -11.27) * mm});
            skPoint(sketch, "E93.4.0", {"position": v(3.75, -63.64) * mm});
            skArc(sketch, "E93.4.1", {"start": v(25.95, -34.18) * mm, "mid": v(29.98, -30.7) * mm, "end": v(33.55, -26.76) * mm});
            skLineSegment(sketch, "E93.4.2", {"start": v(12.84, -26.65) * mm, "end": v(20.25, -42.05) * mm, "construction": true});
            skLineSegment(sketch, "E93.4.3", {"start": v(20.25, -42.05) * mm, "end": v(27.66, -57.44) * mm, "construction": true});
            skArc(sketch, "E93.4.4", {"start": v(21.87, -45.42) * mm, "mid": v(15.08, -48.1) * mm, "end": v(7.96, -49.78) * mm});
            skArc(sketch, "E93.4.5", {"start": v(20.38, -26.38) * mm, "mid": v(23.39, -23.75) * mm, "end": v(26.06, -20.78) * mm});
            skArc(sketch, "E93.4.6", {"start": v(11.2, -23.28) * mm, "mid": v(12.9, -22.38) * mm, "end": v(14.53, -21.36) * mm});
            skLineSegment(sketch, "E93.4.7", {"start": v(8.57, -11.63) * mm, "end": v(14.72, -16.53) * mm});
            skLineSegment(sketch, "E93.4.8", {"start": v(19.93, -32.73) * mm, "end": v(19.22, -31.28) * mm});
            skArc(sketch, "E93.4.9", {"start": v(43.08, -39.15) * mm, "mid": v(44.96, -42.88) * mm, "end": v(43.37, -46.73) * mm});
            skPoint(sketch, "E93.4.10", {"position": v(3.75, -50.28) * mm});
            skArc(sketch, "E93.4.11", {"start": v(27.66, -57.44) * mm, "mid": v(35.91, -52.67) * mm, "end": v(43.37, -46.73) * mm});
            skArc(sketch, "E93.4.12", {"start": v(21.87, -45.42) * mm, "mid": v(28.21, -41.78) * mm, "end": v(33.96, -37.26) * mm});
            skPoint(sketch, "E93.4.13", {"position": v(15.17, -40.15) * mm});
            skLineSegment(sketch, "E93.4.14", {"start": v(5.42, -11.26) * mm, "end": v(12.84, -26.65) * mm, "construction": true});
            skArc(sketch, "E93.4.15", {"start": v(10.55, -41.6) * mm, "mid": v(5.31, -42.59) * mm, "end": v(0, -42.92) * mm});
            skPoint(sketch, "E93.4.16", {"position": v(20.25, -42.05) * mm});
            skLineSegment(sketch, "E93.4.17", {"start": v(3.75, -13.95) * mm, "end": v(3.75, -21.81) * mm});
            skArc(sketch, "E93.4.18", {"start": v(27.66, -57.44) * mm, "mid": v(18.79, -60.92) * mm, "end": v(9.5, -63.04) * mm});
            skLineSegment(sketch, "E93.4.19", {"start": v(40.44, -37.05) * mm, "end": v(43.08, -39.15) * mm});
            skPoint(sketch, "E93.4.20", {"position": v(3.75, -25.56) * mm});
            skArc(sketch, "E93.4.21", {"start": v(7.91, -32.38) * mm, "mid": v(3.99, -33.1) * mm, "end": v(0, -33.33) * mm});
            skPoint(sketch, "E93.4.22", {"position": v(3.75, -11.92) * mm});
            skPoint(sketch, "E93.4.23", {"position": v(11, -31.47) * mm});
            skArc(sketch, "E93.4.24", {"start": v(7.96, -49.78) * mm, "mid": v(4.95, -51.48) * mm, "end": v(3.75, -54.72) * mm});
            skLineSegment(sketch, "E93.4.25", {"start": v(13.17, -35.99) * mm, "end": v(12.47, -34.53) * mm});
            skArc(sketch, "E93.4.26", {"start": v(11.2, -23.28) * mm, "mid": v(9.45, -24.04) * mm, "end": v(7.64, -24.68) * mm});
            skPoint(sketch, "E93.4.27", {"position": v(3.75, -63.64) * mm});
            skArc(sketch, "E93.4.28", {"start": v(10.55, -41.6) * mm, "mid": v(13.19, -39.42) * mm, "end": v(13.17, -35.99) * mm});
            skArc(sketch, "E93.4.29", {"start": v(12.47, -34.53) * mm, "mid": v(10.57, -32.65) * mm, "end": v(7.91, -32.38) * mm});
            skLineSegment(sketch, "E93.4.30", {"start": v(3.75, -54.72) * mm, "end": v(3.75, -58.1) * mm});
            skArc(sketch, "E93.4.31", {"start": v(3.75, -58.1) * mm, "mid": v(5.49, -61.88) * mm, "end": v(9.5, -63.04) * mm});
            skArc(sketch, "E93.4.32", {"start": v(5.4, -11.27) * mm, "mid": v(7.04, -11) * mm, "end": v(8.57, -11.63) * mm});
            skArc(sketch, "E93.4.33", {"start": v(14.72, -16.53) * mm, "mid": v(15.84, -19) * mm, "end": v(14.53, -21.36) * mm});
            skArc(sketch, "E93.4.34", {"start": v(25.95, -34.18) * mm, "mid": v(22.6, -34.89) * mm, "end": v(19.93, -32.73) * mm});
            skArc(sketch, "E93.4.35", {"start": v(19.22, -31.28) * mm, "mid": v(18.94, -28.62) * mm, "end": v(20.38, -26.38) * mm});
            skArc(sketch, "E93.4.36", {"start": v(3.75, -21.81) * mm, "mid": v(4.97, -24.23) * mm, "end": v(7.64, -24.68) * mm});
            skArc(sketch, "E93.4.37", {"start": v(33.96, -37.26) * mm, "mid": v(37.16, -35.96) * mm, "end": v(40.44, -37.05) * mm});
            skArc(sketch, "E93.4.38", {"start": v(5.44, -11.25) * mm, "mid": v(4.2, -12.36) * mm, "end": v(3.75, -13.95) * mm});
            skArc(sketch, "E93.4.39", {"start": v(5.42, -11.26) * mm, "mid": v(-5.41, 11.27) * mm, "end": v(5.4, -11.27) * mm});
            skArc(sketch, "E93.4.40", {"start": v(5.42, -11.26) * mm, "mid": v(-5.43, 11.26) * mm, "end": v(5.44, -11.25) * mm});
            skArc(sketch, "E94.1.5.0", {"start": v(42.9, -1.03) * mm, "mid": v(42.7, 4.3) * mm, "end": v(41.84, 9.55) * mm});
            skLineSegment(sketch, "E94.5.5.0", {"start": v(28.84, -6.58) * mm, "end": v(45.5, -10.38) * mm, "construction": true});
            skLineSegment(sketch, "E94.8.5.0", {"start": v(45.5, -10.38) * mm, "end": v(62.15, -14.19) * mm, "construction": true});
            skPoint(sketch, "E94.10.5.0", {"position": v(52.1, -36.75) * mm});
            skArc(sketch, "E94.11.5.0", {"start": v(49.15, -11.22) * mm, "mid": v(47.01, -18.2) * mm, "end": v(43.89, -24.82) * mm});
            skArc(sketch, "E94.15.5.0", {"start": v(33.33, -0.5) * mm, "mid": v(33.15, 3.48) * mm, "end": v(32.5, 7.42) * mm});
            skArc(sketch, "E94.19.5.0", {"start": v(25.19, -5.75) * mm, "mid": v(25.54, -3.86) * mm, "end": v(25.76, -1.95) * mm});
            skLineSegment(sketch, "E94.23.5.0", {"start": v(14.44, -0.55) * mm, "end": v(22.1, 1.2) * mm});
            skLineSegment(sketch, "E94.26.5.0", {"start": v(38.02, -4.83) * mm, "end": v(36.44, -4.47) * mm});
            skArc(sketch, "E94.29.5.0", {"start": v(57.47, 9.27) * mm, "mid": v(61.55, 8.42) * mm, "end": v(63.57, 4.77) * mm});
            skPoint(sketch, "E94.33.5.0", {"position": v(41.65, -28.42) * mm});
            skArc(sketch, "E94.34.5.0", {"start": v(62.15, -14.19) * mm, "mid": v(63.57, -4.76) * mm, "end": v(63.57, 4.77) * mm});
            skArc(sketch, "E94.38.5.0", {"start": v(49.15, -11.22) * mm, "mid": v(50.26, -4) * mm, "end": v(50.3, 3.32) * mm});
            skPoint(sketch, "E94.42.5.0", {"position": v(40.85, -13.17) * mm});
            skLineSegment(sketch, "E94.43.5.0", {"start": v(12.19, -2.78) * mm, "end": v(28.84, -6.58) * mm, "construction": true});
            skArc(sketch, "E94.46.5.0", {"start": v(39.1, -17.7) * mm, "mid": v(36.6, -22.4) * mm, "end": v(33.55, -26.76) * mm});
            skPoint(sketch, "E94.50.5.0", {"position": v(45.5, -10.38) * mm});
            skLineSegment(sketch, "E94.51.5.0", {"start": v(13.25, -5.77) * mm, "end": v(19.4, -10.67) * mm});
            skArc(sketch, "E94.54.5.0", {"start": v(62.15, -14.19) * mm, "mid": v(59.34, -23.3) * mm, "end": v(55.2, -31.88) * mm});
            skLineSegment(sketch, "E94.58.5.0", {"start": v(54.18, 8.52) * mm, "end": v(57.47, 9.27) * mm});
            skPoint(sketch, "E94.61.5.0", {"position": v(22.32, -13) * mm});
            skArc(sketch, "E94.62.5.0", {"start": v(30.25, -14) * mm, "mid": v(28.36, -17.52) * mm, "end": v(26.06, -20.78) * mm});
            skPoint(sketch, "E94.66.5.0", {"position": v(11.66, -4.5) * mm});
            skPoint(sketch, "E94.67.5.0", {"position": v(31.46, -11.03) * mm});
            skArc(sketch, "E94.68.5.0", {"start": v(43.89, -24.82) * mm, "mid": v(43.33, -28.23) * mm, "end": v(45.12, -31.19) * mm});
            skLineSegment(sketch, "E94.72.5.0", {"start": v(36.35, -12.14) * mm, "end": v(34.77, -11.78) * mm});
            skArc(sketch, "E94.75.5.0", {"start": v(25.19, -5.75) * mm, "mid": v(24.69, -7.6) * mm, "end": v(24.06, -9.42) * mm});
            skPoint(sketch, "E94.79.5.0", {"position": v(52.1, -36.75) * mm});
            skArc(sketch, "E94.80.5.0", {"start": v(39.1, -17.7) * mm, "mid": v(39.04, -14.26) * mm, "end": v(36.35, -12.14) * mm});
            skArc(sketch, "E94.84.5.0", {"start": v(34.77, -11.78) * mm, "mid": v(32.12, -12.1) * mm, "end": v(30.25, -14) * mm});
            skLineSegment(sketch, "E94.88.5.0", {"start": v(45.12, -31.19) * mm, "end": v(47.76, -33.29) * mm});
            skArc(sketch, "E94.91.5.0", {"start": v(47.76, -33.29) * mm, "mid": v(51.8, -34.3) * mm, "end": v(55.2, -31.88) * mm});
            skArc(sketch, "E94.95.5.0", {"start": v(12.18, -2.8) * mm, "mid": v(12.99, -1.35) * mm, "end": v(14.44, -0.55) * mm});
            skArc(sketch, "E94.99.5.0", {"start": v(22.1, 1.2) * mm, "mid": v(24.73, 0.55) * mm, "end": v(25.76, -1.95) * mm});
            skArc(sketch, "E94.103.5.0", {"start": v(42.9, -1.03) * mm, "mid": v(41.36, -4.09) * mm, "end": v(38.02, -4.83) * mm});
            skArc(sketch, "E94.107.5.0", {"start": v(36.44, -4.47) * mm, "mid": v(34.18, -3.04) * mm, "end": v(33.33, -0.5) * mm});
            skArc(sketch, "E94.111.5.0", {"start": v(19.4, -10.67) * mm, "mid": v(22.04, -11.22) * mm, "end": v(24.06, -9.42) * mm});
            skArc(sketch, "E94.115.5.0", {"start": v(50.3, 3.32) * mm, "mid": v(51.29, 6.63) * mm, "end": v(54.18, 8.52) * mm});
            skArc(sketch, "E94.119.5.0", {"start": v(12.2, -2.76) * mm, "mid": v(12.29, -4.42) * mm, "end": v(13.25, -5.77) * mm});
            skArc(sketch, "E94.123.5.0", {"start": v(12.19, -2.78) * mm, "mid": v(-12.18, 2.8) * mm, "end": v(12.18, -2.8) * mm});
            skArc(sketch, "E94.127.5.0", {"start": v(12.19, -2.78) * mm, "mid": v(-12.19, 2.77) * mm, "end": v(12.2, -2.76) * mm});
            skArc(sketch, "E94.1.6.0", {"start": v(27.55, 32.9) * mm, "mid": v(23.27, 36.06) * mm, "end": v(18.62, 38.67) * mm});
            skLineSegment(sketch, "E94.5.6.0", {"start": v(23.13, 18.44) * mm, "end": v(36.49, 29.1) * mm, "construction": true});
            skLineSegment(sketch, "E94.8.6.0", {"start": v(36.49, 29.1) * mm, "end": v(49.84, 39.75) * mm, "construction": true});
            skPoint(sketch, "E94.10.6.0", {"position": v(61.2, 17.82) * mm});
            skArc(sketch, "E94.11.6.0", {"start": v(39.42, 31.43) * mm, "mid": v(43.55, 25.4) * mm, "end": v(46.76, 18.84) * mm});
            skArc(sketch, "E94.15.6.0", {"start": v(21.18, 25.74) * mm, "mid": v(17.95, 28.09) * mm, "end": v(14.46, 30.03) * mm});
            skArc(sketch, "E94.19.6.0", {"start": v(20.2, 16.1) * mm, "mid": v(18.95, 17.56) * mm, "end": v(17.59, 18.92) * mm});
            skLineSegment(sketch, "E94.23.6.0", {"start": v(9.43, 10.94) * mm, "end": v(12.84, 18.03) * mm});
            skLineSegment(sketch, "E94.26.6.0", {"start": v(27.48, 26.71) * mm, "end": v(26.21, 25.7) * mm});
            skArc(sketch, "E94.29.6.0", {"start": v(28.59, 50.71) * mm, "mid": v(31.8, 53.37) * mm, "end": v(35.9, 52.68) * mm});
            skPoint(sketch, "E94.33.6.0", {"position": v(48.18, 14.84) * mm});
            skArc(sketch, "E94.34.6.0", {"start": v(49.84, 39.75) * mm, "mid": v(43.36, 46.73) * mm, "end": v(35.9, 52.68) * mm});
            skArc(sketch, "E94.38.6.0", {"start": v(39.42, 31.43) * mm, "mid": v(34.46, 36.8) * mm, "end": v(28.77, 41.4) * mm});
            skPoint(sketch, "E94.42.6.0", {"position": v(35.76, 23.72) * mm});
            skLineSegment(sketch, "E94.43.6.0", {"start": v(9.77, 7.8) * mm, "end": v(23.13, 18.44) * mm, "construction": true});
            skArc(sketch, "E94.46.6.0", {"start": v(38.21, 19.54) * mm, "mid": v(40.34, 14.66) * mm, "end": v(41.84, 9.55) * mm});
            skPoint(sketch, "E94.50.6.0", {"position": v(36.49, 29.1) * mm});
            skLineSegment(sketch, "E94.51.6.0", {"start": v(12.77, 6.76) * mm, "end": v(20.43, 8.5) * mm});
            skArc(sketch, "E94.54.6.0", {"start": v(49.84, 39.75) * mm, "mid": v(55.21, 31.87) * mm, "end": v(59.35, 23.28) * mm});
            skLineSegment(sketch, "E94.58.6.0", {"start": v(27.12, 47.68) * mm, "end": v(28.59, 50.71) * mm});
            skPoint(sketch, "E94.61.6.0", {"position": v(24.08, 9.34) * mm});
            skArc(sketch, "E94.62.6.0", {"start": v(29.8, 14.92) * mm, "mid": v(31.38, 11.25) * mm, "end": v(32.5, 7.42) * mm});
            skPoint(sketch, "E94.66.6.0", {"position": v(10.8, 6.3) * mm});
            skPoint(sketch, "E94.67.6.0", {"position": v(28.23, 17.72) * mm});
            skArc(sketch, "E94.68.6.0", {"start": v(46.76, 18.84) * mm, "mid": v(49.09, 16.28) * mm, "end": v(52.52, 15.83) * mm});
            skLineSegment(sketch, "E94.72.6.0", {"start": v(32.15, 20.85) * mm, "end": v(30.9, 19.84) * mm});
            skArc(sketch, "E94.75.6.0", {"start": v(20.2, 16.1) * mm, "mid": v(21.34, 14.56) * mm, "end": v(22.36, 12.94) * mm});
            skPoint(sketch, "E94.79.6.0", {"position": v(61.2, 17.82) * mm});
            skArc(sketch, "E94.80.6.0", {"start": v(38.21, 19.54) * mm, "mid": v(35.5, 21.63) * mm, "end": v(32.15, 20.85) * mm});
            skArc(sketch, "E94.84.6.0", {"start": v(30.9, 19.84) * mm, "mid": v(29.48, 17.57) * mm, "end": v(29.8, 14.92) * mm});
            skLineSegment(sketch, "E94.88.6.0", {"start": v(52.52, 15.83) * mm, "end": v(55.8, 16.58) * mm});
            skArc(sketch, "E94.91.6.0", {"start": v(55.8, 16.58) * mm, "mid": v(59.11, 19.12) * mm, "end": v(59.35, 23.28) * mm});
            skArc(sketch, "E94.95.6.0", {"start": v(9.79, 7.78) * mm, "mid": v(9.15, 9.3) * mm, "end": v(9.43, 10.94) * mm});
            skArc(sketch, "E94.99.6.0", {"start": v(12.84, 18.03) * mm, "mid": v(14.99, 19.67) * mm, "end": v(17.59, 18.92) * mm});
            skArc(sketch, "E94.103.6.0", {"start": v(27.55, 32.9) * mm, "mid": v(28.98, 29.79) * mm, "end": v(27.48, 26.71) * mm});
            skArc(sketch, "E94.107.6.0", {"start": v(26.21, 25.7) * mm, "mid": v(23.69, 24.83) * mm, "end": v(21.18, 25.74) * mm});
            skArc(sketch, "E94.111.6.0", {"start": v(20.43, 8.5) * mm, "mid": v(22.51, 10.24) * mm, "end": v(22.36, 12.94) * mm});
            skArc(sketch, "E94.115.6.0", {"start": v(28.77, 41.4) * mm, "mid": v(26.8, 44.23) * mm, "end": v(27.12, 47.68) * mm});
            skArc(sketch, "E94.119.6.0", {"start": v(9.76, 7.81) * mm, "mid": v(11.11, 6.85) * mm, "end": v(12.77, 6.76) * mm});
            skArc(sketch, "E94.123.6.0", {"start": v(9.77, 7.8) * mm, "mid": v(-9.78, -7.78) * mm, "end": v(9.79, 7.78) * mm});
            skArc(sketch, "E94.127.6.0", {"start": v(9.77, 7.8) * mm, "mid": v(-9.77, -7.8) * mm, "end": v(9.76, 7.81) * mm});
            skSolve(sketch);
        }
        {
            var Q0;
            Q0=makeQuery(id+"F8.imprint","IMPRINT",FACE,{"disambiguationData":[TD([[makeQuery(id+"F8.imprint","IMPRINT",EDGE,{"derivedFrom":sQuery(id+"F8.wireOp",EDGE,"E57")}),-1.0]])]});
            var Q1;
            Q1=makeQuery(id+"F8.imprint","IMPRINT",FACE,{"disambiguationData":[TD([[makeQuery(id+"F8.imprint","IMPRINT",EDGE,{"derivedFrom":sQuery(id+"F8.wireOp",EDGE,"E93.1.4")}),1.0]])]});
            var Q2;
            Q2=makeQuery(id+"F8.imprint","IMPRINT",FACE,{"disambiguationData":[TD([[makeQuery(id+"F8.imprint","IMPRINT",EDGE,{"derivedFrom":sQuery(id+"F8.wireOp",EDGE,"E93.2.4")}),1.0]])]});
            var Q3;
            Q3=makeQuery(id+"F8.imprint","IMPRINT",FACE,{"disambiguationData":[TD([[makeQuery(id+"F8.imprint","IMPRINT",EDGE,{"derivedFrom":sQuery(id+"F8.wireOp",EDGE,"E93.3.4")}),1.0]])]});
            var Q4;
            Q4=makeQuery(id+"F8.imprint","IMPRINT",FACE,{"disambiguationData":[TD([[makeQuery(id+"F8.imprint","IMPRINT",EDGE,{"derivedFrom":sQuery(id+"F8.wireOp",EDGE,"E93.4.4")}),1.0]])]});
            var Q5;
            Q5=makeQuery(id+"F8.imprint","IMPRINT",FACE,{"disambiguationData":[TD([[makeQuery(id+"F8.imprint","IMPRINT",EDGE,{"derivedFrom":sQuery(id+"F8.wireOp",EDGE,"E72")}),1.0]])]});
            var Q6;
            Q6=makeQuery(id+"F8.imprint","IMPRINT",FACE,{"disambiguationData":[TD([[makeQuery(id+"F8.imprint","IMPRINT",EDGE,{"derivedFrom":sQuery(id+"F8.wireOp",EDGE,"E79.MirrorCS")}),1.0]])]});
            var Q7;
            Q7=makeQuery(id+"F8.imprint","IMPRINT",FACE,{"disambiguationData":[TD([[makeQuery(id+"F8.imprint","IMPRINT",EDGE,{"derivedFrom":sQuery(id+"F8.wireOp",EDGE,"E93.1.1")}),1.0]])]});
            var Q8;
            Q8=makeQuery(id+"F8.imprint","IMPRINT",FACE,{"disambiguationData":[TD([[makeQuery(id+"F8.imprint","IMPRINT",EDGE,{"derivedFrom":sQuery(id+"F8.wireOp",EDGE,"E93.2.1")}),1.0]])]});
            var Q9;
            Q9=makeQuery(id+"F8.imprint","IMPRINT",FACE,{"disambiguationData":[TD([[makeQuery(id+"F8.imprint","IMPRINT",EDGE,{"derivedFrom":sQuery(id+"F8.wireOp",EDGE,"E93.3.1")}),1.0]])]});
            var Q10;
            Q10=makeQuery(id+"F8.imprint","IMPRINT",FACE,{"disambiguationData":[TD([[makeQuery(id+"F8.imprint","IMPRINT",EDGE,{"derivedFrom":sQuery(id+"F8.wireOp",EDGE,"E93.4.6")}),1.0]])]});
            var Q11;
            Q11=makeQuery(id+"F8.imprint","IMPRINT",FACE,{"disambiguationData":[TD([[makeQuery(id+"F8.imprint","IMPRINT",EDGE,{"derivedFrom":sQuery(id+"F8.wireOp",EDGE,"E55")}),1.0]])]});
            var Q12;
            Q12=makeQuery(id+"F8.imprint","IMPRINT",FACE,{"disambiguationData":[TD([[makeQuery(id+"F8.imprint","IMPRINT",EDGE,{"derivedFrom":sQuery(id+"F8.wireOp",EDGE,"E93.1.6")}),1.0]])]});
            var Q13;
            Q13=makeQuery(id+"F8.imprint","IMPRINT",FACE,{"disambiguationData":[TD([[makeQuery(id+"F8.imprint","IMPRINT",EDGE,{"derivedFrom":sQuery(id+"F8.wireOp",EDGE,"E93.2.6")}),1.0]])]});
            var Q14;
            Q14=makeQuery(id+"F8.imprint","IMPRINT",FACE,{"disambiguationData":[TD([[makeQuery(id+"F8.imprint","IMPRINT",EDGE,{"derivedFrom":sQuery(id+"F8.wireOp",EDGE,"E93.3.6")}),1.0]])]});
            var Q15;
            Q15=makeQuery(id+"F8.imprint","IMPRINT",FACE,{"disambiguationData":[TD([[makeQuery(id+"F8.imprint","IMPRINT",EDGE,{"derivedFrom":sQuery(id+"F8.wireOp",EDGE,"E50")}),1.0]])]});
            var Q16;
            Q16=makeQuery(id+"F8.imprint","IMPRINT",FACE,{"disambiguationData":[TD([[makeQuery(id+"F8.imprint","IMPRINT",EDGE,{"derivedFrom":sQuery(id+"F8.wireOp",EDGE,"E94.19.6.0")}),1.0]])]});
            var Q17;
            Q17=makeQuery(id+"F8.imprint","IMPRINT",FACE,{"disambiguationData":[TD([[makeQuery(id+"F8.imprint","IMPRINT",EDGE,{"derivedFrom":sQuery(id+"F8.wireOp",EDGE,"E94.19.5.0")}),1.0]])]});
            var Q18;
            Q18=makeQuery(id+"F8.imprint","IMPRINT",FACE,{"disambiguationData":[TD([[makeQuery(id+"F8.imprint","IMPRINT",EDGE,{"derivedFrom":sQuery(id+"F8.wireOp",EDGE,"E93.4.1")}),1.0]])]});
            var Q19;
            Q19=makeQuery(id+"F8.imprint","IMPRINT",FACE,{"disambiguationData":[TD([[makeQuery(id+"F8.imprint","IMPRINT",EDGE,{"derivedFrom":sQuery(id+"F8.wireOp",EDGE,"E94.1.5.0")}),1.0]])]});
            var Q20;
            Q20=makeQuery(id+"F8.imprint","IMPRINT",FACE,{"disambiguationData":[TD([[makeQuery(id+"F8.imprint","IMPRINT",EDGE,{"derivedFrom":sQuery(id+"F8.wireOp",EDGE,"E94.11.6.0")}),1.0]])]});
            var Q21;
            Q21=makeQuery(id+"F8.imprint","IMPRINT",FACE,{"disambiguationData":[TD([[makeQuery(id+"F8.imprint","IMPRINT",EDGE,{"derivedFrom":sQuery(id+"F8.wireOp",EDGE,"E94.11.5.0")}),1.0]])]});
            extrude(context, id + "F9", {"entities" : qUnion([Q0, Q1, Q2, Q3, Q4, Q5, Q6, Q7, Q8, Q9, Q10, Q11, Q12, Q13, Q14, Q15, Q16, Q17, Q18, Q19, Q20, Q21]), "operationType" : NewBodyOperationType.REMOVE, "endBound" : BoundingType.THROUGH_ALL, "oppositeDirection" : true, "depth" : 25 * mm, "hasSecondDirection" : true, "secondDirectionBound" : SecondDirectionBoundingType.THROUGH_ALL, "secondDirectionOppositeDirection" : false, "secondDirectionDepth" : 25 * mm});
        }
        {
            var Q0;
            Q0=makeQuery(id+"F8.imprint","IMPRINT",FACE,{"disambiguationData":[TD([[makeQuery(id+"F8.imprint","IMPRINT",EDGE,{"derivedFrom":sQuery(id+"F8.wireOp",EDGE,"E50")}),-1.0]])]});
            extrude(context, id + "F10", {"entities" : qUnion([Q0]), "operationType" : NewBodyOperationType.ADD, "endBound" : BoundingType.SYMMETRIC, "depth" : 5 * mm});
        }
        {
            var Q0;
            Q0=qCreatedBy(makeId("Top.planeOp"),FACE);
            var sketch = newSketch(context, id + "F11", { "sketchPlane" : qUnion([Q0])});
            skCircle(sketch, "E95.0", {"center": v(0, 0) * mm, "radius": 78 * mm});
            skCircle(sketch, "E95.1", {"center": v(0, 0) * mm, "radius": 75 * mm});
            skCircle(sketch, "E95.2", {"center": v(0, 0) * mm, "radius": 70.48 * mm});
            skCircle(sketch, "E95.3", {"center": v(0, 0) * mm, "radius": 83 * mm});
            skLineSegment(sketch, "E95.4", {"start": v(-3.61, 77.92) * mm, "end": v(0, 0) * mm, "construction": true});
            skFitSpline(sketch, "E95.5", {"points": [v(-6.52, 70.17) * mm, v(-6.52, 70.24) * mm, v(-6.52, 70.2) * mm, v(-6.53, 70.48) * mm, v(-6.52, 70.78) * mm, v(-6.5, 71.26) * mm, v(-6.43, 71.86) * mm, v(-6.33, 72.59) * mm, v(-6.16, 73.45) * mm, v(-5.93, 74.42) * mm, v(-5.61, 75.52) * mm, v(-5.21, 76.73) * mm, v(-4.7, 78.05) * mm, v(-4.1, 79.46) * mm, v(-3.36, 80.97) * mm, v(-2.5, 82.57) * mm, v(-1.5, 84.23) * mm, v(-0.35, 85.97) * mm, v(0.95, 87.76) * mm, v(2.41, 89.6) * mm, v(4.04, 91.48) * mm, v(5.84, 93.38) * mm, v(7.82, 95.3) * mm, v(9.97, 97.2) * mm, v(12.32, 99.1) * mm, v(14.86, 100.99) * mm, v(17.56, 102.82) * mm, v(20.56, 104.65) * mm, v(23.33, 106.22) * mm, v(27.95, 108.48) * mm, v(26.9, 107.97) * mm, v(30.4, 109.53) * mm], "construction": true});
            skFitSpline(sketch, "E95.6", {"points": [v(0, 70.48) * mm, v(0, 70.54) * mm, v(0, 70.51) * mm, v(-0.02, 70.78) * mm, v(-0.05, 71.08) * mm, v(-0.12, 71.56) * mm, v(-0.24, 72.15) * mm, v(-0.42, 72.86) * mm, v(-0.66, 73.7) * mm, v(-0.98, 74.65) * mm, v(-1.4, 75.72) * mm, v(-1.91, 76.88) * mm, v(-2.53, 78.15) * mm, v(-3.28, 79.5) * mm, v(-4.15, 80.94) * mm, v(-5.15, 82.44) * mm, v(-6.3, 84.01) * mm, v(-7.6, 85.63) * mm, v(-9.07, 87.3) * mm, v(-10.7, 89) * mm, v(-12.48, 90.71) * mm, v(-14.45, 92.44) * mm, v(-16.6, 94.16) * mm, v(-18.92, 95.87) * mm, v(-21.43, 97.54) * mm, v(-24.14, 99.18) * mm, v(-27, 100.75) * mm, v(-30.16, 102.3) * mm, v(-33.05, 103.6) * mm, v(-37.87, 105.43) * mm, v(-36.78, 105.02) * mm, v(-40.4, 106.24) * mm], "construction": true});
            skCircle(sketch, "E96", {"center": v(0, 0) * mm, "radius": 93.6 * mm});
            skLineSegment(sketch, "E97", {"start": v(0, 0) * mm, "end": v(1.55, 93.59) * mm, "construction": true});
            skLineSegment(sketch, "E98", {"start": v(0, 0) * mm, "end": v(-10.2, 93.04) * mm, "construction": true});
            skLineSegment(sketch, "E99", {"start": v(-10.2, 93.04) * mm, "end": v(-7.68, 70.06) * mm});
            skLineSegment(sketch, "E100", {"start": v(1.16, 70.47) * mm, "end": v(1.55, 93.59) * mm});
            skFitSpline(sketch, "E101.0", {"points": [v(0.05, 70.48) * mm, v(0.05, 70.52) * mm, v(0.05, 70.54) * mm, v(0.05, 70.55) * mm, v(0.04, 70.6) * mm, v(0.04, 70.68) * mm, v(0.03, 70.77) * mm, v(0.02, 70.89) * mm, v(0, 71.03) * mm, v(-0.02, 71.21) * mm, v(-0.05, 71.42) * mm, v(-0.09, 71.63) * mm, v(-0.15, 71.93) * mm, v(-0.23, 72.33) * mm, v(-0.36, 72.83) * mm, v(-0.5, 73.36) * mm, v(-0.74, 74.1) * mm, v(-1.08, 75.06) * mm, v(-1.58, 76.27) * mm, v(-2.16, 77.53) * mm, v(-3.06, 79.24) * mm, v(-4.39, 81.45) * mm, v(-6.3, 84.14) * mm, v(-8.54, 86.82) * mm, v(-11.07, 89.47) * mm, v(-13.41, 91.62) * mm, v(-15.42, 93.29) * mm, v(-17, 94.52) * mm, v(-18.64, 95.71) * mm, v(-20.34, 96.88) * mm, v(-22.1, 98) * mm, v(-23.92, 99.1) * mm, v(-25.48, 99.98) * mm, v(-26.76, 100.66) * mm, v(-27.75, 101.17) * mm, v(-28.75, 101.66) * mm, v(-29.74, 102.14) * mm, v(-30.7, 102.6) * mm, v(-31.5, 102.96) * mm, v(-32.2, 103.26) * mm, v(-32.73, 103.49) * mm, v(-33.31, 103.72) * mm, v(-33.94, 103.97) * mm, v(-34.58, 104.23) * mm, v(-35.2, 104.47) * mm, v(-35.77, 104.69) * mm, v(-36.27, 104.88) * mm, v(-36.6, 105) * mm, v(-36.78, 105.07) * mm, v(-36.92, 105.12) * mm, v(-37.03, 105.17) * mm, v(-37.2, 105.22) * mm, v(-37.49, 105.32) * mm, v(-38.2, 105.56) * mm, v(-39.28, 105.92) * mm, v(-40.38, 106.3) * mm]});
            skFitSpline(sketch, "E102.0", {"points": [v(-6.57, 70.17) * mm, v(-6.57, 70.2) * mm, v(-6.57, 70.23) * mm, v(-6.57, 70.24) * mm, v(-6.58, 70.3) * mm, v(-6.58, 70.38) * mm, v(-6.58, 70.47) * mm, v(-6.58, 70.58) * mm, v(-6.58, 70.72) * mm, v(-6.57, 70.9) * mm, v(-6.55, 71.12) * mm, v(-6.54, 71.33) * mm, v(-6.5, 71.64) * mm, v(-6.46, 72.04) * mm, v(-6.38, 72.55) * mm, v(-6.28, 73.1) * mm, v(-6.12, 73.85) * mm, v(-5.87, 74.84) * mm, v(-5.49, 76.09) * mm, v(-5.02, 77.4) * mm, v(-4.29, 79.19) * mm, v(-3.17, 81.5) * mm, v(-1.5, 84.36) * mm, v(0.47, 87.24) * mm, v(2.74, 90.11) * mm, v(4.88, 92.47) * mm, v(6.73, 94.32) * mm, v(8.18, 95.68) * mm, v(9.7, 97.03) * mm, v(11.29, 98.34) * mm, v(12.94, 99.63) * mm, v(14.65, 100.89) * mm, v(16.12, 101.9) * mm, v(17.33, 102.7) * mm, v(18.27, 103.3) * mm, v(19.22, 103.89) * mm, v(20.16, 104.46) * mm, v(21.08, 105) * mm, v(21.85, 105.43) * mm, v(22.5, 105.8) * mm, v(23.02, 106.07) * mm, v(23.58, 106.36) * mm, v(24.17, 106.67) * mm, v(24.79, 106.98) * mm, v(25.38, 107.28) * mm, v(25.94, 107.55) * mm, v(26.41, 107.78) * mm, v(26.72, 107.93) * mm, v(26.9, 108.02) * mm, v(27.04, 108.09) * mm, v(27.15, 108.14) * mm, v(27.3, 108.2) * mm, v(27.58, 108.33) * mm, v(28.28, 108.64) * mm, v(29.31, 109.1) * mm, v(30.38, 109.57) * mm]});
            skSolve(sketch);
        }
        {
            var Q0;
            {var subQ1=sQuery(id+"F11.wireOp",EDGE,"E99");var subQ5=sQuery(id+"F11.wireOp",EDGE,"E96");var subQ6=makeQuery(id+"F11.imprint","INTERSECT",VERTEX,{"derivedFrom":[subQ5,subQ1]});Q0=makeQuery(id+"F11.imprint","IMPRINT",FACE,{"disambiguationData":[TD([[makeQuery(id+"F11.imprint","IMPRINT",EDGE,{"disambiguationData":[TD([[subQ6,1.0]])],"derivedFrom":subQ5}),1.0]])]});}
            var Q1;
            {var subQ0=sQuery(id+"F11.wireOp",EDGE,"E102.0");var subQ1=sQuery(id+"F11.wireOp",EDGE,"E95.0");var subQ2=makeQuery(id+"F11.imprint","INTERSECT",VERTEX,{"derivedFrom":[subQ1,subQ0]});Q1=makeQuery(id+"F11.imprint","IMPRINT",FACE,{"disambiguationData":[TD([[makeQuery(id+"F11.imprint","IMPRINT",EDGE,{"disambiguationData":[TD([[subQ2,-1.0]])],"derivedFrom":subQ1}),-1.0]])]});}
            var Q2;
            {var subQ0=sQuery(id+"F11.wireOp",EDGE,"E101.0");var subQ1=sQuery(id+"F11.wireOp",EDGE,"E95.0");var subQ2=makeQuery(id+"F11.imprint","INTERSECT",VERTEX,{"derivedFrom":[subQ1,subQ0]});Q2=makeQuery(id+"F11.imprint","IMPRINT",FACE,{"disambiguationData":[TD([[makeQuery(id+"F11.imprint","IMPRINT",EDGE,{"disambiguationData":[TD([[subQ2,1.0]])],"derivedFrom":subQ1}),-1.0]])]});}
            var Q3;
            {var subQ0=sQuery(id+"F11.wireOp",EDGE,"E102.0");var subQ1=sQuery(id+"F11.wireOp",EDGE,"E95.0");var subQ2=makeQuery(id+"F11.imprint","INTERSECT",VERTEX,{"derivedFrom":[subQ1,subQ0]});Q3=makeQuery(id+"F11.imprint","IMPRINT",FACE,{"disambiguationData":[TD([[makeQuery(id+"F11.imprint","IMPRINT",EDGE,{"disambiguationData":[TD([[subQ2,-1.0]])],"derivedFrom":subQ1}),1.0]])]});}
            var Q4;
            {var subQ0=sQuery(id+"F11.wireOp",EDGE,"E101.0");var subQ1=sQuery(id+"F11.wireOp",EDGE,"E95.0");var subQ2=makeQuery(id+"F11.imprint","INTERSECT",VERTEX,{"derivedFrom":[subQ1,subQ0]});Q4=makeQuery(id+"F11.imprint","IMPRINT",FACE,{"disambiguationData":[TD([[makeQuery(id+"F11.imprint","IMPRINT",EDGE,{"disambiguationData":[TD([[subQ2,1.0]])],"derivedFrom":subQ1}),1.0]])]});}
            var Q5;
            {var subQ0=sQuery(id+"F11.wireOp",EDGE,"E102.0");var subQ1=sQuery(id+"F11.wireOp",EDGE,"E95.1");var subQ2=makeQuery(id+"F11.imprint","INTERSECT",VERTEX,{"derivedFrom":[subQ1,subQ0]});Q5=makeQuery(id+"F11.imprint","IMPRINT",FACE,{"disambiguationData":[TD([[makeQuery(id+"F11.imprint","IMPRINT",EDGE,{"disambiguationData":[TD([[subQ2,-1.0]])],"derivedFrom":subQ1}),1.0]])]});}
            var Q6;
            {var subQ0=sQuery(id+"F11.wireOp",EDGE,"E101.0");var subQ1=sQuery(id+"F11.wireOp",EDGE,"E95.1");var subQ2=makeQuery(id+"F11.imprint","INTERSECT",VERTEX,{"derivedFrom":[subQ1,subQ0]});Q6=makeQuery(id+"F11.imprint","IMPRINT",FACE,{"disambiguationData":[TD([[makeQuery(id+"F11.imprint","IMPRINT",EDGE,{"disambiguationData":[TD([[subQ2,1.0]])],"derivedFrom":subQ1}),1.0]])]});}
            var Q7;
            {var subQ0=sQuery(id+"F11.wireOp",EDGE,"E101.0");var subQ1=sQuery(id+"F11.wireOp",EDGE,"E95.0");var subQ2=makeQuery(id+"F11.imprint","INTERSECT",VERTEX,{"derivedFrom":[subQ1,subQ0]});Q7=makeQuery(id+"F11.imprint","IMPRINT",FACE,{"disambiguationData":[TD([[makeQuery(id+"F11.imprint","IMPRINT",EDGE,{"disambiguationData":[TD([[subQ2,-1.0]])],"derivedFrom":subQ1}),-1.0]])]});}
            extrude(context, id + "F12", {"entities" : qUnion([Q0, Q1, Q2, Q3, Q4, Q5, Q6, Q7]), "endBound" : BoundingType.SYMMETRIC, "depth" : getVariable(context, 'Thickness')});
        }
        {
            var Q0;
            Q0=makeQuery(id+"F12.opExtrude","SWEPT_EDGE",EDGE,{"disambiguationData":[OSD([sQuery(id+"F11.wireOp",EDGE,"E95.3"),sQuery(id+"F11.wireOp",EDGE,"E102.0")])]});
            var Q1;
            Q1=makeQuery(id+"F12.opExtrude","SWEPT_EDGE",EDGE,{"disambiguationData":[OSD([sQuery(id+"F11.wireOp",EDGE,"E95.3"),sQuery(id+"F11.wireOp",EDGE,"E101.0")])]});
            fillet(context, id + "F13", {"entities" : qUnion([Q0, Q1]), "radius" : getVariable(context, 'Mod') * 0.3, "tangentPropagation" : true, "allowEdgeOverflow" : false});
        }
        {
            var Q0;
            Q0=makeQuery(id+"F12.opExtrude","SWEPT_BODY",BODY,{"disambiguationData":[OSD([sQuery(id+"F11.wireOp",EDGE,"E95.0"),sQuery(id+"F11.wireOp",EDGE,"E95.2"),sQuery(id+"F11.wireOp",EDGE,"E95.5"),sQuery(id+"F11.wireOp",EDGE,"E95.6"),sQuery(id+"F11.wireOp",EDGE,"E96"),sQuery(id+"F11.wireOp",EDGE,"E99"),sQuery(id+"F11.wireOp",EDGE,"E100")])]});
            var Q1;
            Q1=sQuery(id+"F6.wireOp",EDGE,"E48");
            circularPattern(context, id + "F14", {"operationType" : NewBodyOperationType.ADD, "entities" : qUnion([Q0]), "axis" : qUnion([Q1]), "angle" : 360 * degree, "instanceCount" : getVariable(context, 'T'), "equalSpace" : true});
        }
    });
